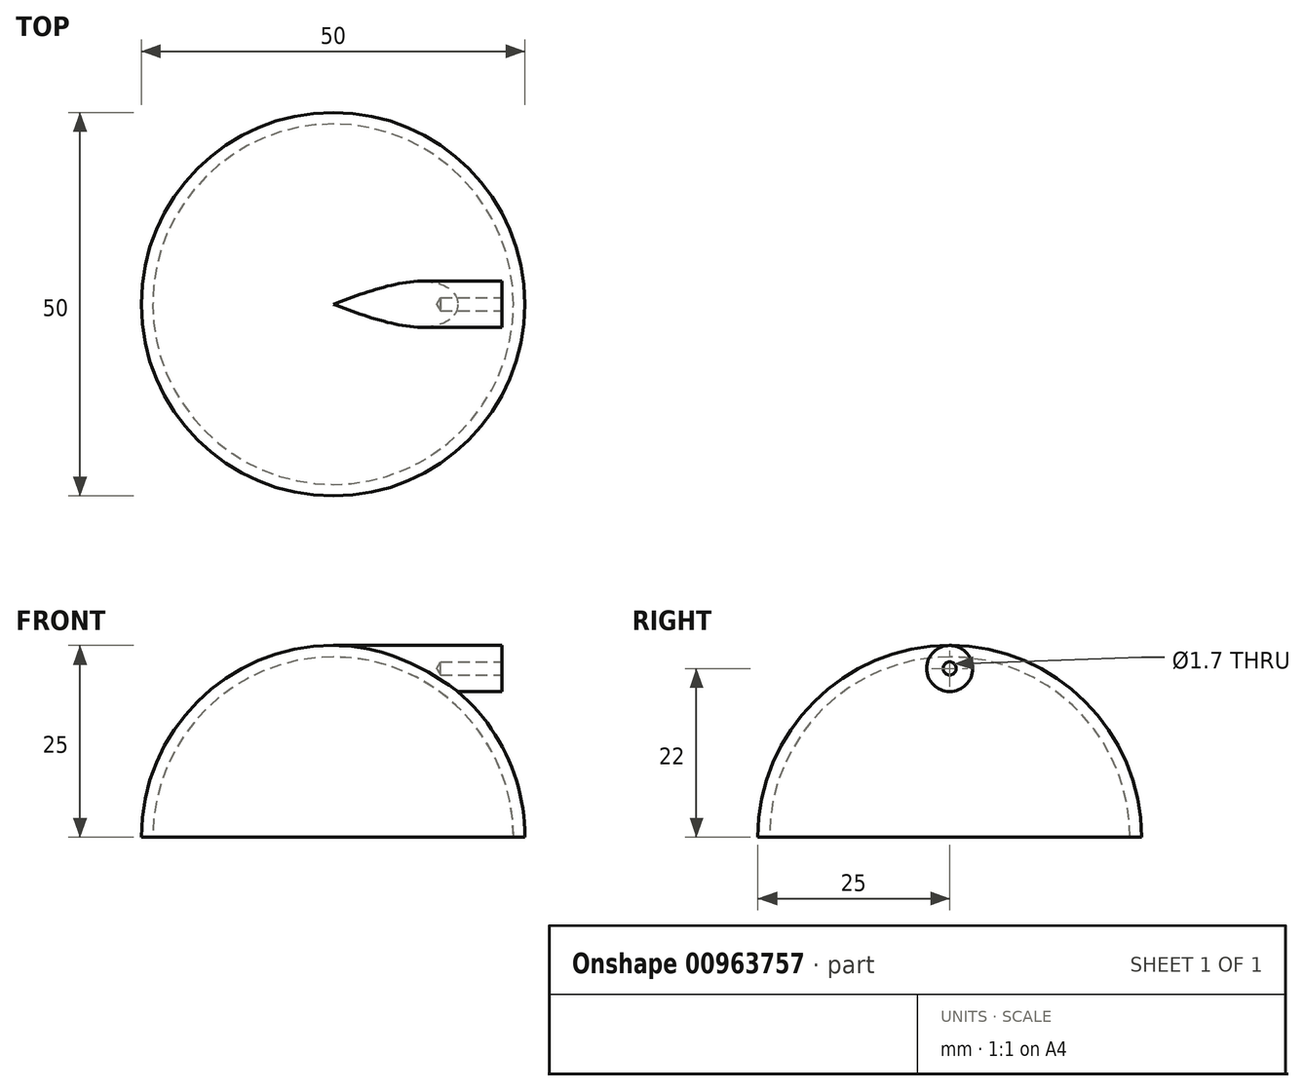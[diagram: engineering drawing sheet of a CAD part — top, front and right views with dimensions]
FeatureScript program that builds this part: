
annotation { "Feature Type Name" : "Feature", "Feature Type Description" : "" }
export const myFeature = defineFeature(function(context is Context, id is Id, definition is map)
    precondition{}
    {
        {
            var Q0;
            Q0=qCreatedBy(makeId("Top.planeOp"),FACE);
            var sketch = newSketch(context, id + "F0", { "sketchPlane" : qUnion([Q0])});
            skCircle(sketch, "E0", {"center": v(0, 0) * mm, "radius": 25 * mm});
            skSolve(sketch);
        }
        {
            var Q0;
            Q0 = qSketchRegion(id + "F0", true);
            extrude(context, id + "F1", {"entities" : qUnion([Q0]), "depth" : 25 * mm, "offsetDistance" : 25 * mm});
        }
        {
            var Q0;
            Q0=makeQuery(id+"F1.opExtrude","CAP_EDGE",EDGE,{"disambiguationData":[OSD([sQuery(id+"F0.wireOp",EDGE,"E0")])],"isStart":false});
            fillet(context, id + "F2", {"entities" : qUnion([Q0]), "radius" : 25 * mm, "tangentPropagation" : true, "allowEdgeOverflow" : false});
        }
        {
            var Q0;
            Q0=qCreatedBy(makeId("Right.planeOp"),FACE);
            var sketch = newSketch(context, id + "F3", { "sketchPlane" : qUnion([Q0])});
            skLineSegment(sketch, "E1", {"start": v(0, 0) * mm, "end": v(0, 22) * mm, "construction": true});
            skCircle(sketch, "E2", {"center": v(0, 22) * mm, "radius": 3 * mm});
            skSolve(sketch);
        }
        {
            var Q0;
            Q0 = qSketchRegion(id + "F3", true);
            extrude(context, id + "F4", {"entities" : qUnion([Q0]), "operationType" : NewBodyOperationType.ADD, "depth" : 22 * mm, "offsetDistance" : 25 * mm});
        }
        {
            var Q0;
            Q0=makeQuery(id+"F1.opExtrude","CAP_FACE",FACE,{"disambiguationData":[OSD([sQuery(id+"F0.wireOp",EDGE,"E0")])],"isStart":true});
            var Q1;
            Q1=makeQuery(id+"F4.opExtrude","SWEPT_FACE",FACE,{"disambiguationData":[OSD([sQuery(id+"F3.wireOp",EDGE,"E2")])]});
            var Q2;
            Q2=makeQuery(id+"F1.opExtrude","SWEPT_BODY",BODY,{"disambiguationData":[OSD([sQuery(id+"F0.wireOp",EDGE,"E0")])]});
            shell(context, id + "F5", {"entities" : qUnion([Q0, Q1]), "parts" : qUnion([Q2]), "thickness" : 1.5 * mm});
        }
        {
            var Q0;
            Q0=makeQuery(id+"F4.opExtrude","CAP_FACE",FACE,{"disambiguationData":[OSD([sQuery(id+"F3.wireOp",EDGE,"E2")])],"isStart":false});
            var sketch = newSketch(context, id + "F6", { "sketchPlane" : qUnion([Q0])});
            skPoint(sketch, "E3", {"position": v(0, 22) * mm});
            skSolve(sketch);
        }
        {
            var Q0;
            Q0=sQuery(id+"F6.wireOp",VERTEX,"E3");
            var Q1;
            Q1=makeQuery(id+"F1.opExtrude","SWEPT_BODY",BODY,{"disambiguationData":[OSD([sQuery(id+"F0.wireOp",EDGE,"E0")])]});
            hole(context, id + "F7", {"style" : HoleStyle.SIMPLE, "endStyle" : HoleEndStyle.BLIND, "holeDiameter" : 1.7 * mm, "majorDiameter" : 5 * mm, "holeDepth" : 8 * mm, "isTappedThrough" : true, "tappedDepth" : 12 * mm, "tapClearance" : 3, "locations" : qUnion([Q0]), "scope" : qUnion([Q1])});
        }
    });
